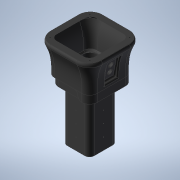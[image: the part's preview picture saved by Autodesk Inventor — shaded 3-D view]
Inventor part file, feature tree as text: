
AUTODESK INVENTOR PART (.ipt)
format: ipt  version: 2021 (Build 250183000, 183)  size: 1,236,480 bytes
history: native  units: mm
features: sketch x26, extrude x13, projected_geometry x12, hole x8, other x6, mirror x4, plane x3, chamfer x3, fillet x3, loft x2, shell x1, sweep x1, pattern_circular x1
ambient origin geometry x8: Origin, YZ Plane, XZ Plane, XY Plane, X Axis, Y Axis, Z Axis, Center Point
bodies: Body1 (feature_tree), Body2 (feature_tree), Body3 (feature_tree), Body4 (feature_tree)
feature tree (83):
  other  "實體1"
  sketch  "草圖1"
  plane  "工作平面1"
  sketch  "草圖2"
  extrude  "擠出1"  Depth=139.0mm
  loft  "斷面混成1"
  extrude  "擠出2"  Depth=25.0mm
  plane  "工作平面2"
  extrude  "擠出6"  Depth=30.0mm
  loft  "斷面混成3"
  chamfer  "倒角2"  Distance=205.0mm
  fillet  "圓角3"  Radius=45.0mm
  extrude  "擠出7"  Depth=240.0mm TaperAngle=0.0deg
  fillet  "圓角4"  [1 undecoded]
  shell  "薄殼2"  Thickness=0.0mm
  chamfer  "倒角1"  Distance=200.0mm
  extrude  "擠出9"  [1 undecoded]
  chamfer  "倒角4"  Distance=220.0mm
  hole  "孔4"  [1 undecoded]
  sweep  "掃掠3"
  hole  "孔6"  [1 undecoded]
  extrude  "擠出10"  Depth=30.0mm
  plane  "工作平面3"
  extrude  "擠出11"  Depth=10.0mm TaperAngle=75.0deg
  fillet  "圓角5"  Radius=20.0mm
  hole  "孔7"  [1 undecoded]
  extrude  "擠出13"  Depth=50.0mm
  extrude  "擠出14"  Depth=40.0mm TaperAngle=0.0deg
  extrude  "擠出15"  Depth=20.0mm
  hole  "孔8"  [1 undecoded]
  mirror  "鏡射1"
  mirror  "鏡射2"
  extrude  "擠出16"  Depth=2.0mm TaperAngle=45.0deg
  extrude  "擠出17"  Depth=10.0mm TaperAngle=45.0deg
  mirror  "鏡射3"
  mirror  "鏡射4"
  hole  "孔9"  [1 undecoded]
  hole  "孔10"  [1 undecoded]
  pattern_circular  "環形陣列2"  [2 undecoded]
  extrude  "擠出18"  Depth=20.0mm TaperAngle=45.0deg
  hole  "孔11"  [1 undecoded]
  hole  "孔12"  [1 undecoded]
  sketch  "草圖3"
  projected_geometry  "投影迴路1"
  sketch  "草圖17"
  sketch  "草圖18"
  projected_geometry  "投影迴路7"
  sketch  "草圖20"
  projected_geometry  "投影迴路9"
  sketch  "草圖23"
  projected_geometry  "投影迴路10"
  sketch  "草圖24"
  sketch  "草圖25"
  sketch  "3D 草圖2"
  sketch  "草圖27"
  sketch  "草圖28"
  other  "Srf1"
  sketch  "草圖29"
  sketch  "草圖30"
  projected_geometry  "投影迴路11"
  sketch  "草圖31"
  sketch  "草圖33"
  projected_geometry  "投影迴路14"
  sketch  "草圖34"
  projected_geometry  "投影迴路15"
  sketch  "草圖35"
  projected_geometry  "投影迴路16"
  sketch  "草圖36"
  sketch  "草圖37"
  projected_geometry  "投影迴路17"
  other  "實體3"
  sketch  "草圖38"
  sketch  "草圖39"
  sketch  "草圖40"
  sketch  "草圖41"
  projected_geometry  "投影迴路18"
  other  "實體4"
  sketch  "草圖42"
  projected_geometry  "投影迴路19"
  sketch  "草圖43"
  projected_geometry  "投影迴路20"
  other  "擠出表面1"
  other  "投影切割邊5"
note: 12 required parameter values undecoded (feature->parameter linkage not recoverable at this tier; creation-order binding heuristic only, values carry confidence <= 0.55)
